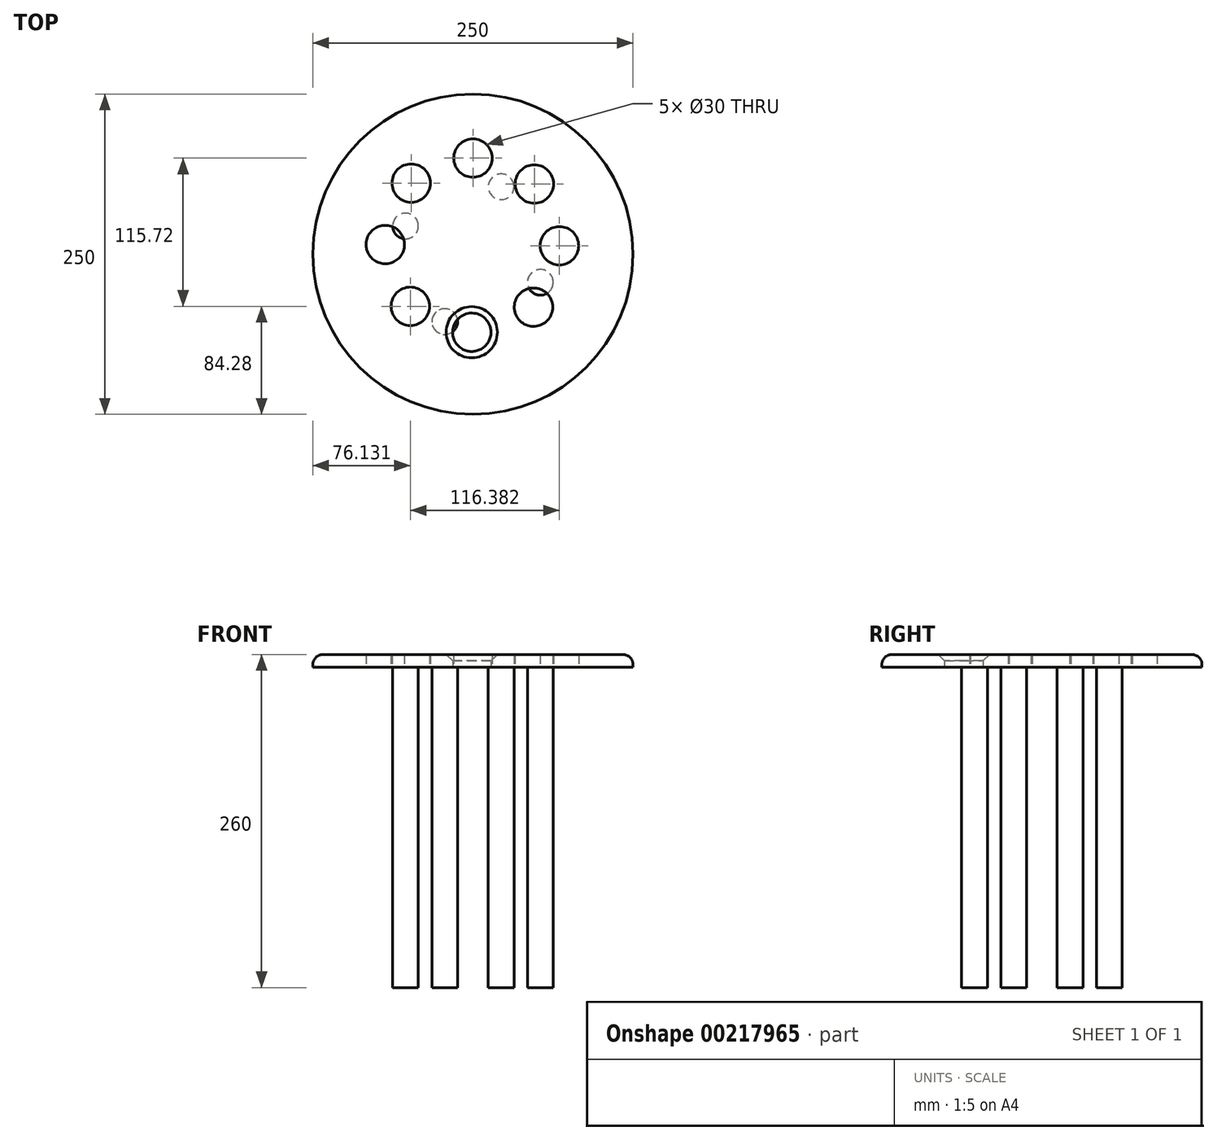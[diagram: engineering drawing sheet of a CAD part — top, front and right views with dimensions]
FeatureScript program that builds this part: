
annotation { "Feature Type Name" : "Feature", "Feature Type Description" : "" }
export const myFeature = defineFeature(function(context is Context, id is Id, definition is map)
    precondition{}
    {
        {
            var Q0;
            Q0=qCreatedBy(makeId("Top.planeOp"),FACE);
            var sketch = newSketch(context, id + "F0", { "sketchPlane" : qUnion([Q0])});
            skCircle(sketch, "E0", {"center": v(0, 0) * mm, "radius": 125 * mm});
            skSolve(sketch);
        }
        {
            var Q0;
            Q0=makeQuery(id+"F0.imprint","IMPRINT",FACE,{"disambiguationData":[TD([[makeQuery(id+"F0.imprint","IMPRINT",EDGE,{"derivedFrom":sQuery(id+"F0.wireOp",EDGE,"E0")}),1.0]])]});
            var sketch = newSketch(context, id + "F1", { "sketchPlane" : qUnion([Q0])});
            skCircle(sketch, "E1", {"center": v(0, 75) * mm, "radius": 15 * mm});
            skCircle(sketch, "E2.1.0", {"center": v(-48.2, 55.42) * mm, "radius": 15 * mm});
            skCircle(sketch, "E2.2.0", {"center": v(-68.45, 7.49) * mm, "radius": 15 * mm});
            skCircle(sketch, "E2.3.0", {"center": v(-48.87, -40.72) * mm, "radius": 15 * mm});
            skCircle(sketch, "E2.4.0", {"center": v(-0.94, -60.96) * mm, "radius": 15 * mm});
            skCircle(sketch, "E2.5.0", {"center": v(47.27, -41.38) * mm, "radius": 15 * mm});
            skCircle(sketch, "E2.6.0", {"center": v(67.51, 6.55) * mm, "radius": 15 * mm});
            skCircle(sketch, "E2.7.0", {"center": v(47.93, 54.76) * mm, "radius": 15 * mm});
            skPoint(sketch, "E2.center", {"position": v(-0.47, 7.02) * mm});
            skSolve(sketch);
        }
        {
            var Q0;
            Q0=makeQuery(id+"F1.imprint","IMPRINT",FACE,{"disambiguationData":[TD([[makeQuery(id+"F1.imprint","IMPRINT",EDGE,{"derivedFrom":sQuery(id+"F1.wireOp",EDGE,"E1")}),-1.0]])]});
            extrude(context, id + "F2", {"entities" : qUnion([Q0]), "depth" : 10 * mm});
        }
        {
            var Q0;
            Q0=makeQuery(id+"F2.opExtrude","CAP_EDGE",EDGE,{"disambiguationData":[OSD([sQuery(id+"F0.wireOp",EDGE,"E0")])],"isStart":false});
            fillet(context, id + "F3", {"entities" : qUnion([Q0]), "radius" : 8 * mm, "tangentPropagation" : true, "allowEdgeOverflow" : false});
        }
        {
            var Q0;
            Q0=makeQuery(id+"F2.opExtrude","CAP_EDGE",EDGE,{"disambiguationData":[OSD([sQuery(id+"F1.wireOp",EDGE,"E2.4.0")])],"isStart":false});
            chamfer(context, id + "F4", {"entities" : qUnion([Q0]), "width" : 5 * mm, "tangentPropagation" : true});
        }
        {
            var Q0;
            Q0=makeQuery(id+"F0.imprint","IMPRINT",FACE,{"disambiguationData":[TD([[makeQuery(id+"F0.imprint","IMPRINT",EDGE,{"derivedFrom":sQuery(id+"F0.wireOp",EDGE,"E0")}),1.0]])]});
            var sketch = newSketch(context, id + "F5", { "sketchPlane" : qUnion([Q0])});
            skCircle(sketch, "E3", {"center": v(-22, -52.64) * mm, "radius": 10.05 * mm});
            skCircle(sketch, "E4.1.0", {"center": v(52.64, -22) * mm, "radius": 10.05 * mm});
            skCircle(sketch, "E4.2.0", {"center": v(22, 52.64) * mm, "radius": 10.05 * mm});
            skCircle(sketch, "E4.3.0", {"center": v(-52.64, 22) * mm, "radius": 10.05 * mm});
            skPoint(sketch, "E4.center", {"position": v(0, 0) * mm});
            skSolve(sketch);
        }
        {
            var Q0;
            Q0=makeQuery(id+"F5.imprint","IMPRINT",FACE,{"disambiguationData":[TD([[makeQuery(id+"F5.imprint","IMPRINT",EDGE,{"derivedFrom":sQuery(id+"F5.wireOp",EDGE,"E4.1.0")}),1.0]])]});
            extrude(context, id + "F6", {"entities" : qUnion([Q0]), "operationType" : NewBodyOperationType.ADD, "oppositeDirection" : true, "depth" : 250 * mm});
        }
        {
            var Q0;
            Q0 = qSketchRegion(id + "F5", true);
            extrude(context, id + "F7", {"entities" : qUnion([Q0]), "operationType" : NewBodyOperationType.ADD, "oppositeDirection" : true, "depth" : 250 * mm});
        }
    });
